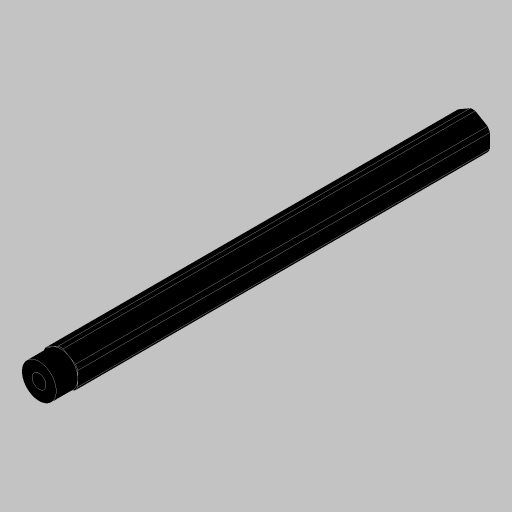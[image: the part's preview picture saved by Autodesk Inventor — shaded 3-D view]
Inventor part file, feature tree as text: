
AUTODESK INVENTOR PART (.ipt)
format: ipt  version: 2023.5 (Build 275446000, 446)  size: 142,336 bytes
history: native  units: in
note: dims shown in document units (in); Inventor stores cm internally (conversion verified against a paired STEP export)
features: extrude x3, projected_geometry x3, hole x1, sketch x1
ambient origin geometry x8: Origin, YZ Plane, XZ Plane, XY Plane, X Axis, Y Axis, Z Axis, Center Point
bodies: Solid1 (feature_tree)
feature tree (8):
  extrude  "Extrusion1"  Depth=0.315in
  hole  "Hole1"  [1 undecoded]
  extrude  "Extrusion3"  Depth=0.5in
  extrude  "Extrusion4"  Depth=0.315in TaperAngle=0.0deg
  sketch  "Sketch5"  dims[d2=0.0in d9=0.625in d10=0.385in d11=0.25in d12=0.5635in d13=1.0in d14=0.8108in d16=0.7in d17=0.0in d18=0.0in d19=0.5in d20=0.315in d21=0.0in]
  projected_geometry  "Project Cut Edges1"
  projected_geometry  "Project Cut Edges2"
  projected_geometry  "Project Cut Edges3"
note: 1 required parameter value undecoded (feature->parameter linkage not recoverable at this tier; creation-order binding heuristic only, values carry confidence <= 0.55)
